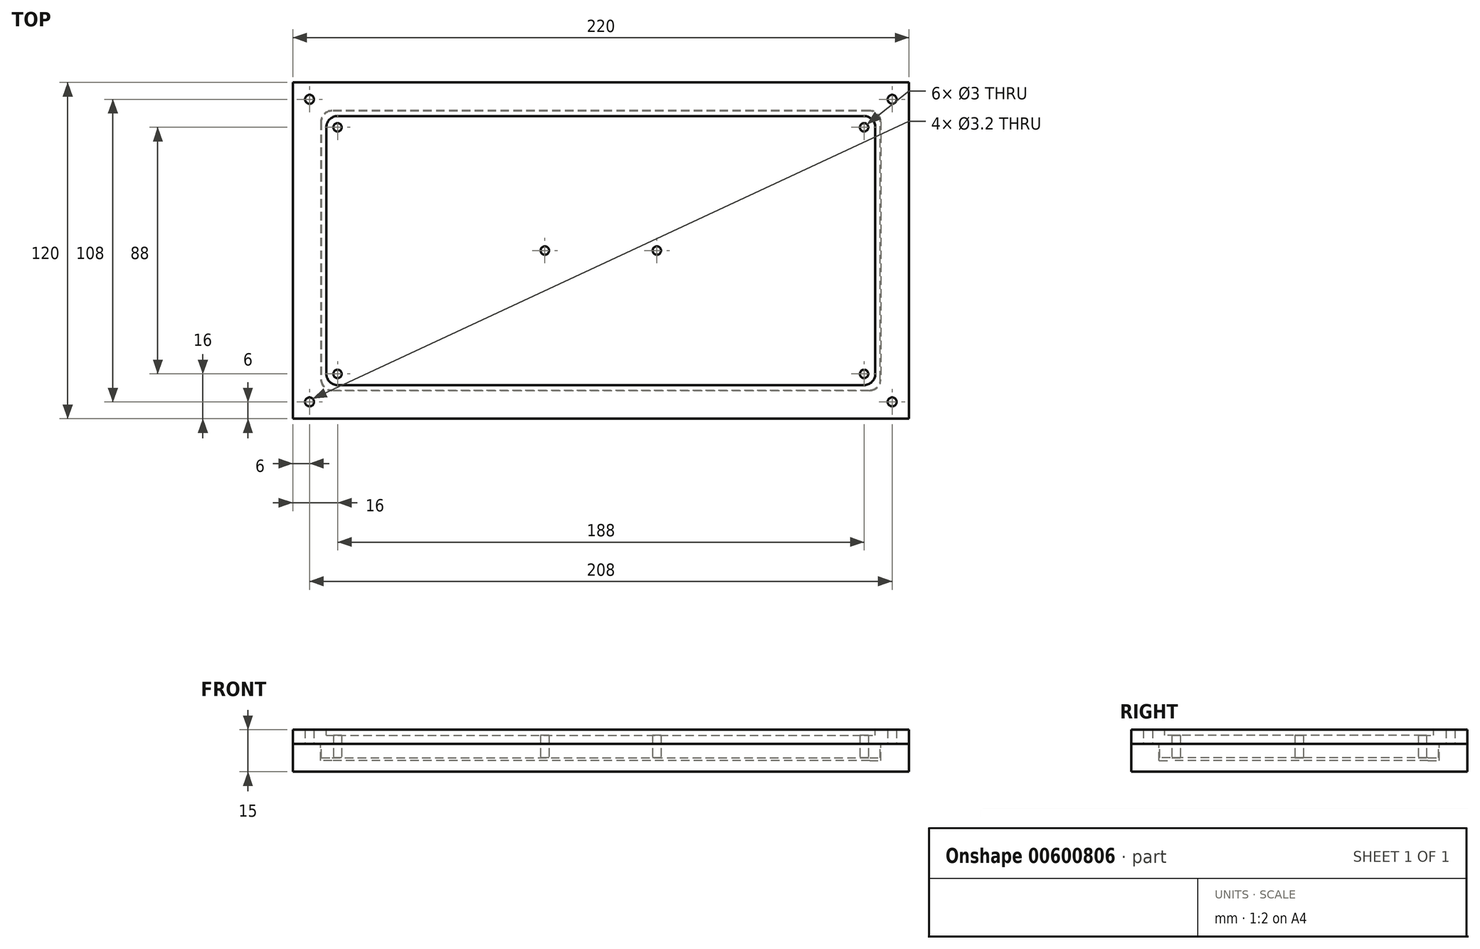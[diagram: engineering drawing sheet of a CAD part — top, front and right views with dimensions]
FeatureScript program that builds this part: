
annotation { "Feature Type Name" : "Feature", "Feature Type Description" : "" }
export const myFeature = defineFeature(function(context is Context, id is Id, definition is map)
    precondition{}
    {
        {
            var Q0;
            Q0=qCreatedBy(makeId("Top.planeOp"),FACE);
            var sketch = newSketch(context, id + "F0", { "sketchPlane" : qUnion([Q0])});
            skLineSegment(sketch, "E0.bottom", {"start": v(110, 60) * mm, "end": v(-110, 60) * mm});
            skLineSegment(sketch, "E0.top", {"start": v(110, -60) * mm, "end": v(-110, -60) * mm});
            skLineSegment(sketch, "E0.left", {"start": v(110, 60) * mm, "end": v(110, -60) * mm});
            skLineSegment(sketch, "E0.right", {"start": v(-110, 60) * mm, "end": v(-110, -60) * mm});
            skPoint(sketch, "E0.middle", {"position": v(0, 0) * mm});
            skLineSegment(sketch, "E1.bottom", {"start": v(96, 50) * mm, "end": v(-96, 50) * mm});
            skLineSegment(sketch, "E1.top", {"start": v(96, -50) * mm, "end": v(-96, -50) * mm});
            skLineSegment(sketch, "E1.left", {"start": v(100, 46) * mm, "end": v(100, -46) * mm});
            skLineSegment(sketch, "E1.right", {"start": v(-100, 46) * mm, "end": v(-100, -46) * mm});
            skPoint(sketch, "E2.visualSharp", {"position": v(100, 50) * mm});
            skArc(sketch, "E2.filletArc", {"start": v(100, 46) * mm, "mid": v(98.83, 48.83) * mm, "end": v(96, 50) * mm});
            skPoint(sketch, "E3.visualSharp", {"position": v(100, -50) * mm});
            skArc(sketch, "E3.filletArc", {"start": v(96, -50) * mm, "mid": v(98.83, -48.83) * mm, "end": v(100, -46) * mm});
            skPoint(sketch, "E4.visualSharp", {"position": v(-100, -50) * mm});
            skArc(sketch, "E4.filletArc", {"start": v(-100, -46) * mm, "mid": v(-98.83, -48.83) * mm, "end": v(-96, -50) * mm});
            skPoint(sketch, "E5.visualSharp", {"position": v(-100, 50) * mm});
            skArc(sketch, "E5.filletArc", {"start": v(-96, 50) * mm, "mid": v(-98.83, 48.83) * mm, "end": v(-100, 46) * mm});
            skSolve(sketch);
        }
        {
            var Q0;
            Q0=makeQuery(id+"F0.imprint","IMPRINT",FACE,{"disambiguationData":[TD([[makeQuery(id+"F0.imprint","IMPRINT",EDGE,{"derivedFrom":sQuery(id+"F0.wireOp",EDGE,"E1.bottom")}),1.0]])]});
            var Q1;
            Q1=makeQuery(id+"F0.imprint","IMPRINT",FACE,{"disambiguationData":[TD([[makeQuery(id+"F0.imprint","IMPRINT",EDGE,{"derivedFrom":sQuery(id+"F0.wireOp",EDGE,"E0.bottom")}),1.0]])]});
            extrude(context, id + "F1", {"entities" : qUnion([Q0, Q1]), "oppositeDirection" : true, "depth" : 10 * mm, "offsetDistance" : 25 * mm});
        }
        {
            var Q0;
            Q0=makeQuery(id+"F0.imprint","IMPRINT",FACE,{"disambiguationData":[TD([[makeQuery(id+"F0.imprint","IMPRINT",EDGE,{"derivedFrom":sQuery(id+"F0.wireOp",EDGE,"E1.bottom")}),1.0]])]});
            extrude(context, id + "F2", {"entities" : qUnion([Q0]), "operationType" : NewBodyOperationType.REMOVE, "oppositeDirection" : true, "depth" : 6 * mm, "offsetDistance" : 25 * mm});
        }
        {
            var Q0;
            Q0=qCreatedBy(makeId("Top.planeOp"),FACE);
            var sketch = newSketch(context, id + "F3", { "sketchPlane" : qUnion([Q0])});
            skArc(sketch, "E6.0", {"start": v(-99.75, -46) * mm, "mid": v(-98.65, -48.65) * mm, "end": v(-96, -49.75) * mm});
            skLineSegment(sketch, "E6.1", {"start": v(-99.75, 46) * mm, "end": v(-99.75, -46) * mm});
            skLineSegment(sketch, "E6.2", {"start": v(-96, -49.75) * mm, "end": v(96, -49.75) * mm});
            skArc(sketch, "E6.3", {"start": v(-96, 49.75) * mm, "mid": v(-98.65, 48.65) * mm, "end": v(-99.75, 46) * mm});
            skArc(sketch, "E6.4", {"start": v(96, -49.75) * mm, "mid": v(98.65, -48.65) * mm, "end": v(99.75, -46) * mm});
            skLineSegment(sketch, "E6.5", {"start": v(99.75, -46) * mm, "end": v(99.75, 46) * mm});
            skArc(sketch, "E6.6", {"start": v(99.75, 46) * mm, "mid": v(98.65, 48.65) * mm, "end": v(96, 49.75) * mm});
            skLineSegment(sketch, "E6.7", {"start": v(96, 49.75) * mm, "end": v(-96, 49.75) * mm});
            skLineSegment(sketch, "E7.bottom", {"start": v(-110, 60) * mm, "end": v(110, 60) * mm});
            skLineSegment(sketch, "E7.top", {"start": v(-110, -60) * mm, "end": v(110, -60) * mm});
            skLineSegment(sketch, "E7.left", {"start": v(-110, 60) * mm, "end": v(-110, -60) * mm});
            skLineSegment(sketch, "E7.right", {"start": v(110, 60) * mm, "end": v(110, -60) * mm});
            skPoint(sketch, "E7.middle", {"position": v(0, 0) * mm});
            skLineSegment(sketch, "E8.bottom", {"start": v(-104, 54) * mm, "end": v(104, 54) * mm, "construction": true});
            skLineSegment(sketch, "E8.top", {"start": v(-104, -54) * mm, "end": v(104, -54) * mm, "construction": true});
            skLineSegment(sketch, "E8.left", {"start": v(-104, 54) * mm, "end": v(-104, -54) * mm, "construction": true});
            skLineSegment(sketch, "E8.right", {"start": v(104, 54) * mm, "end": v(104, -54) * mm, "construction": true});
            skCircle(sketch, "E9", {"center": v(-104, 54) * mm, "radius": 1.6 * mm});
            skCircle(sketch, "E10", {"center": v(-104, -54) * mm, "radius": 1.6 * mm});
            skCircle(sketch, "E11", {"center": v(104, -54) * mm, "radius": 1.6 * mm});
            skCircle(sketch, "E12", {"center": v(104, 54) * mm, "radius": 1.6 * mm});
            skLineSegment(sketch, "E13.bottom", {"start": v(-94, 44) * mm, "end": v(94, 44) * mm, "construction": true});
            skLineSegment(sketch, "E13.top", {"start": v(-94, -44) * mm, "end": v(94, -44) * mm, "construction": true});
            skLineSegment(sketch, "E13.left", {"start": v(-94, 44) * mm, "end": v(-94, -44) * mm, "construction": true});
            skLineSegment(sketch, "E13.right", {"start": v(94, 44) * mm, "end": v(94, -44) * mm, "construction": true});
            skCircle(sketch, "E14", {"center": v(-94, 44) * mm, "radius": 1.5 * mm});
            skCircle(sketch, "E15", {"center": v(94, 44) * mm, "radius": 1.5 * mm});
            skCircle(sketch, "E16", {"center": v(94, -44) * mm, "radius": 1.5 * mm});
            skCircle(sketch, "E17", {"center": v(-94, -44) * mm, "radius": 1.5 * mm});
            skCircle(sketch, "E18", {"center": v(-20, 0) * mm, "radius": 1.5 * mm});
            skCircle(sketch, "E19", {"center": v(20, 0) * mm, "radius": 1.5 * mm});
            skSolve(sketch);
        }
        {
            var Q0;
            Q0 = qSketchRegion(id + "F3", true);
            var Q1;
            Q1=makeQuery(id+"F3.imprint","IMPRINT",FACE,{"disambiguationData":[TD([[makeQuery(id+"F3.imprint","IMPRINT",EDGE,{"derivedFrom":sQuery(id+"F3.wireOp",EDGE,"E6.0")}),1.0]])]});
            extrude(context, id + "F4", {"entities" : qUnion([Q0, Q1]), "depth" : 5 * mm, "offsetDistance" : 25 * mm});
        }
        {
            var Q0;
            Q0=makeQuery(id+"F3.imprint","IMPRINT",FACE,{"disambiguationData":[TD([[makeQuery(id+"F3.imprint","IMPRINT",EDGE,{"derivedFrom":sQuery(id+"F3.wireOp",EDGE,"E6.0")}),1.0]])]});
            extrude(context, id + "F5", {"entities" : qUnion([Q0]), "operationType" : NewBodyOperationType.ADD, "oppositeDirection" : true, "depth" : 5 * mm, "offsetDistance" : 25 * mm});
        }
        {
            var Q0;
            Q0=makeQuery(id+"F4.opExtrude","CAP_FACE",FACE,{"disambiguationData":[OSD([sQuery(id+"F3.wireOp",EDGE,"E7.bottom"),sQuery(id+"F3.wireOp",EDGE,"E7.top"),sQuery(id+"F3.wireOp",EDGE,"E7.left"),sQuery(id+"F3.wireOp",EDGE,"E7.right"),sQuery(id+"F3.wireOp",EDGE,"E9"),sQuery(id+"F3.wireOp",EDGE,"E10"),sQuery(id+"F3.wireOp",EDGE,"E11"),sQuery(id+"F3.wireOp",EDGE,"E12"),sQuery(id+"F3.wireOp",EDGE,"E14"),sQuery(id+"F3.wireOp",EDGE,"E15"),sQuery(id+"F3.wireOp",EDGE,"E16"),sQuery(id+"F3.wireOp",EDGE,"E17"),sQuery(id+"F3.wireOp",EDGE,"E18"),sQuery(id+"F3.wireOp",EDGE,"E19")])],"isStart":false});
            var sketch = newSketch(context, id + "F6", { "sketchPlane" : qUnion([Q0])});
            skLineSegment(sketch, "E20.bottom", {"start": v(-94, 48) * mm, "end": v(94, 48) * mm});
            skLineSegment(sketch, "E20.top", {"start": v(-94, -48) * mm, "end": v(94, -48) * mm});
            skLineSegment(sketch, "E20.left", {"start": v(-98, 44) * mm, "end": v(-98, -44) * mm});
            skLineSegment(sketch, "E20.right", {"start": v(98, 44) * mm, "end": v(98, -44) * mm});
            skPoint(sketch, "E20.middle", {"position": v(0, 0) * mm});
            skPoint(sketch, "E21.visualSharp", {"position": v(-98, 48) * mm});
            skArc(sketch, "E21.filletArc", {"start": v(-94, 48) * mm, "mid": v(-96.83, 46.83) * mm, "end": v(-98, 44) * mm});
            skPoint(sketch, "E22.visualSharp", {"position": v(-98, -48) * mm});
            skArc(sketch, "E22.filletArc", {"start": v(-98, -44) * mm, "mid": v(-96.83, -46.83) * mm, "end": v(-94, -48) * mm});
            skPoint(sketch, "E23.visualSharp", {"position": v(98, -48) * mm});
            skArc(sketch, "E23.filletArc", {"start": v(94, -48) * mm, "mid": v(96.83, -46.83) * mm, "end": v(98, -44) * mm});
            skPoint(sketch, "E24.visualSharp", {"position": v(98, 48) * mm});
            skArc(sketch, "E24.filletArc", {"start": v(98, 44) * mm, "mid": v(96.83, 46.83) * mm, "end": v(94, 48) * mm});
            skSolve(sketch);
        }
        {
            var Q0;
            Q0 = qSketchRegion(id + "F6", true);
            extrude(context, id + "F7", {"entities" : qUnion([Q0]), "operationType" : NewBodyOperationType.REMOVE, "oppositeDirection" : true, "depth" : 2 * mm, "offsetDistance" : 25 * mm});
        }
    });
